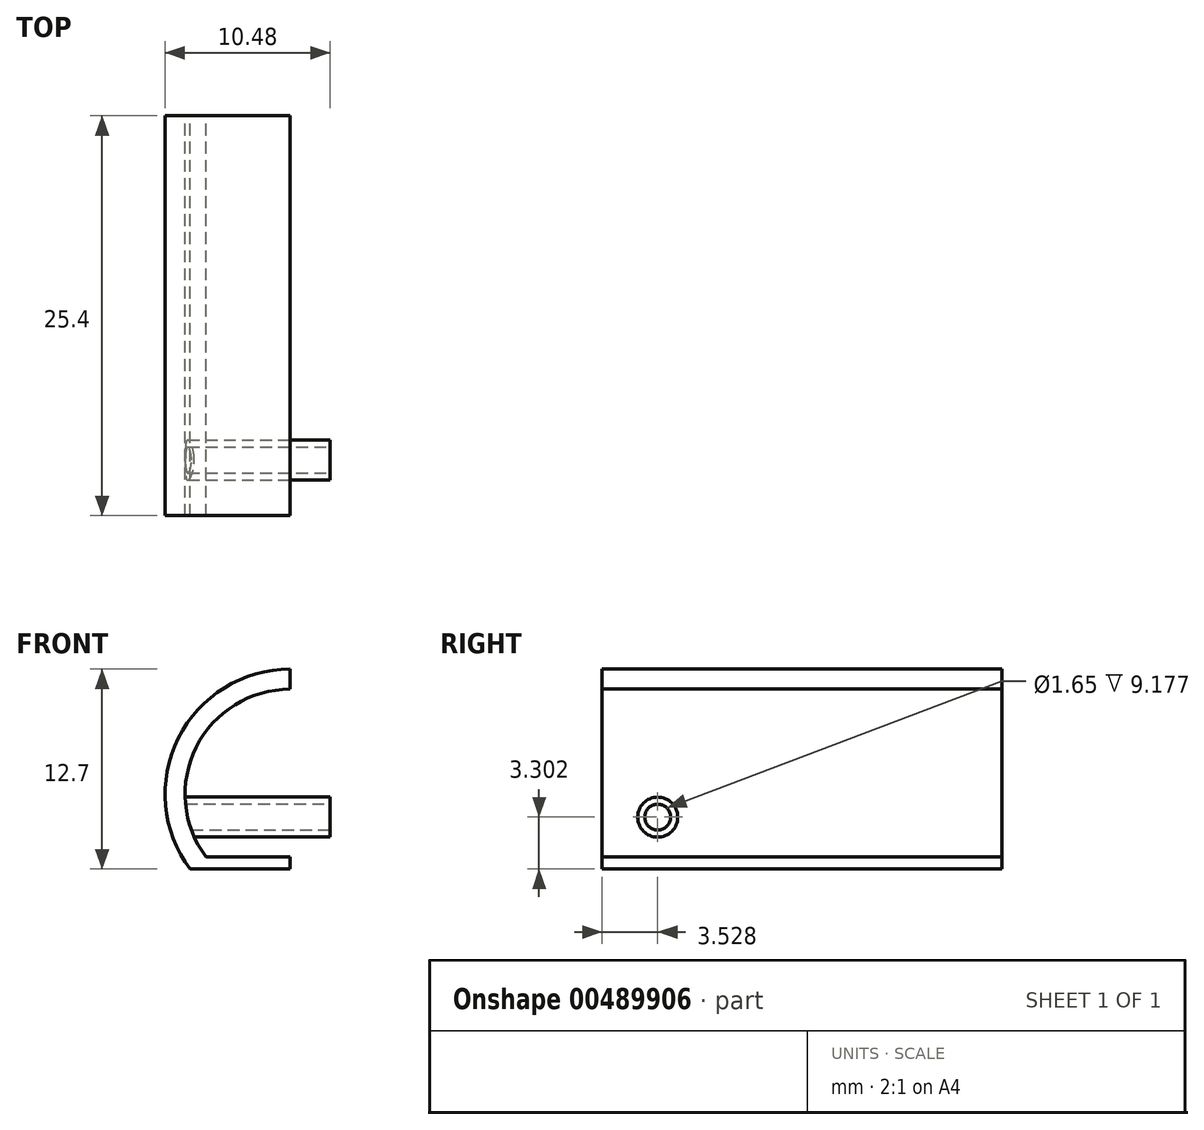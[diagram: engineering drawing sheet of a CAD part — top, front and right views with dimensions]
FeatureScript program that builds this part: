
annotation { "Feature Type Name" : "Feature", "Feature Type Description" : "" }
export const myFeature = defineFeature(function(context is Context, id is Id, definition is map)
    precondition{}
    {
        {
            var Q0;
            Q0=qCreatedBy(makeId("Front.planeOp"),FACE);
            var sketch = newSketch(context, id + "F0", { "sketchPlane" : qUnion([Q0])});
            skLineSegment(sketch, "E0", {"start": v(0, 0) * mm, "end": v(-6.35, 0) * mm});
            skArc(sketch, "E1", {"start": v(0, 12.7) * mm, "mid": v(-7.1, 8.31) * mm, "end": v(-6.35, 0) * mm});
            skArc(sketch, "E2.0", {"start": v(0, 11.43) * mm, "mid": v(-5.96, 7.74) * mm, "end": v(-5.33, 0.76) * mm});
            skLineSegment(sketch, "E3", {"start": v(-5.33, 0.76) * mm, "end": v(0, 0.76) * mm});
            skLineSegment(sketch, "E4", {"start": v(0, 0.76) * mm, "end": v(0, 0) * mm});
            skLineSegment(sketch, "E5", {"start": v(0, 11.43) * mm, "end": v(0, 12.7) * mm});
            skSolve(sketch);
        }
        {
            var Q0;
            Q0 = qSketchRegion(id + "F0", true);
            extrude(context, id + "F1", {"entities" : qUnion([Q0]), "depth" : 25.4 * mm});
        }
        {
            var Q0;
            Q0=qCreatedBy(makeId("Right.planeOp"),FACE);
            var sketch = newSketch(context, id + "F2", { "sketchPlane" : qUnion([Q0])});
            skCircle(sketch, "E6", {"center": v(-21.87, 3.3) * mm, "radius": 1.27 * mm});
            skCircle(sketch, "E7", {"center": v(-21.87, 3.3) * mm, "radius": 0.83 * mm});
            skSolve(sketch);
        }
        {
            var Q0;
            Q0 = qSketchRegion(id + "F2", true);
            extrude(context, id + "F3", {"entities" : qUnion([Q0]), "operationType" : NewBodyOperationType.ADD, "oppositeDirection" : true, "depth" : 7.11 * mm});
        }
        {
            var Q0;
            Q0=makeQuery(id+"F3.opExtrude","CAP_FACE",FACE,{"disambiguationData":[OSD([sQuery(id+"F2.wireOp",EDGE,"E6")])],"isStart":true});
            extrude(context, id + "F4", {"entities" : qUnion([Q0]), "operationType" : NewBodyOperationType.ADD, "depth" : 2.54 * mm});
        }
    });
